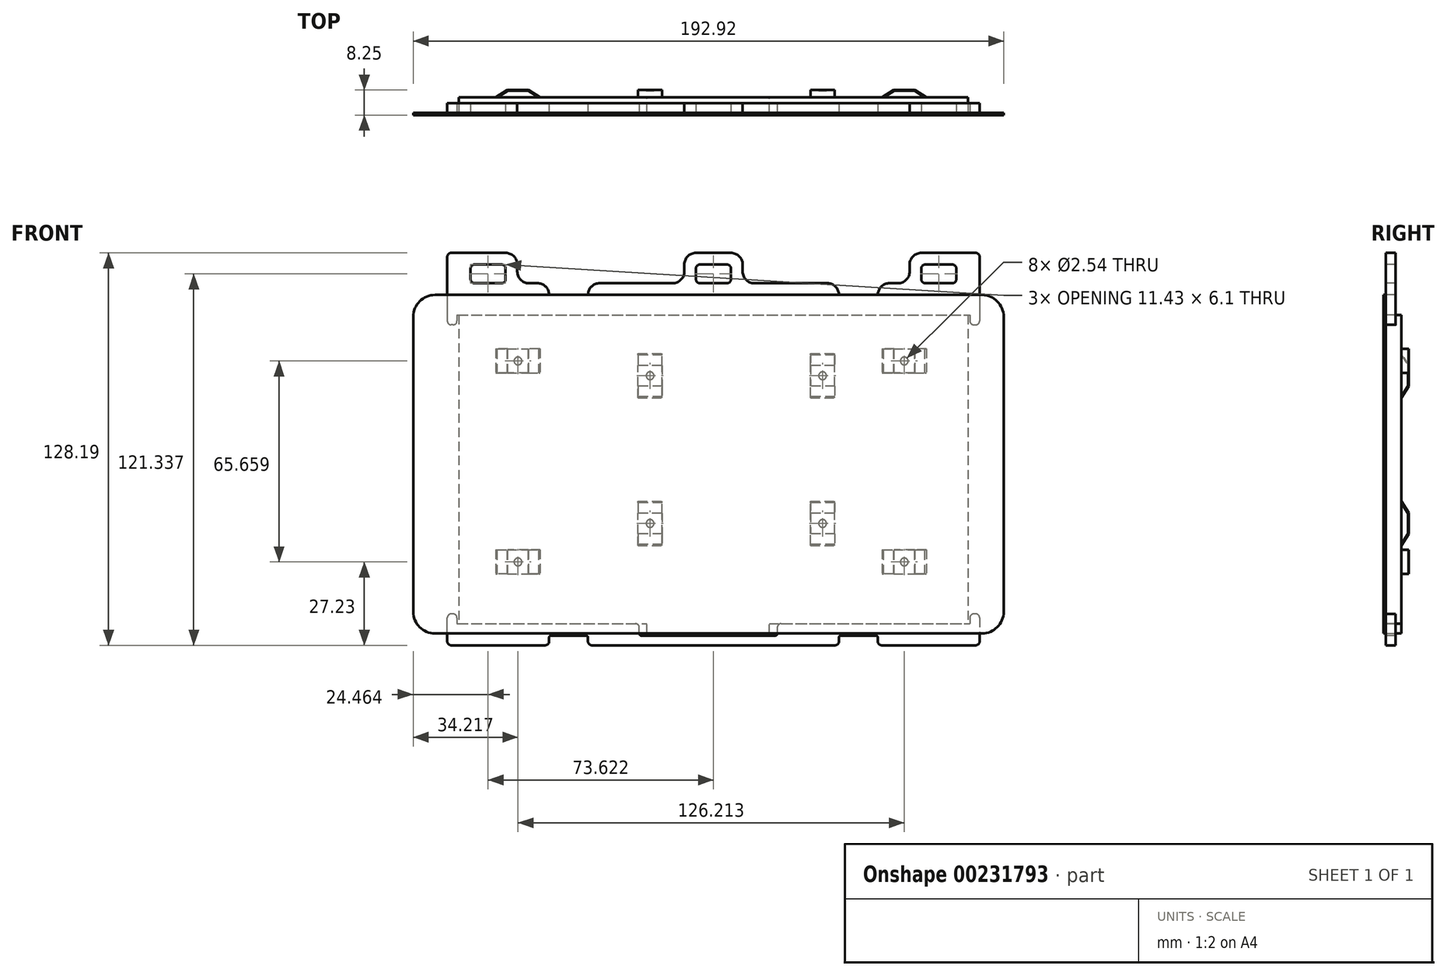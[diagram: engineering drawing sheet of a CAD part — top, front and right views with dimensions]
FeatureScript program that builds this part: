
annotation { "Feature Type Name" : "Feature", "Feature Type Description" : "" }
export const myFeature = defineFeature(function(context is Context, id is Id, definition is map)
    precondition{}
    {
        {
            var Q0;
            Q0=qCreatedBy(makeId("Front.planeOp"),FACE);
            var sketch = newSketch(context, id + "F0", { "sketchPlane" : qUnion([Q0])});
            skLineSegment(sketch, "E0.bottom", {"start": v(89.34, 55.3) * mm, "end": v(-89.34, 55.3) * mm});
            skLineSegment(sketch, "E0.top", {"start": v(89.34, -55.3) * mm, "end": v(-89.34, -55.3) * mm});
            skLineSegment(sketch, "E0.left", {"start": v(96.46, 48.2) * mm, "end": v(96.46, -48.2) * mm});
            skLineSegment(sketch, "E0.right", {"start": v(-96.46, 48.2) * mm, "end": v(-96.46, -48.2) * mm});
            skPoint(sketch, "E0.middle", {"position": v(0, 0) * mm});
            skPoint(sketch, "E1.visualSharp", {"position": v(-96.46, 55.3) * mm});
            skArc(sketch, "E1.filletArc", {"start": v(-89.34, 55.3) * mm, "mid": v(-94.37, 53.23) * mm, "end": v(-96.46, 48.2) * mm});
            skPoint(sketch, "E2.visualSharp", {"position": v(-96.46, -55.3) * mm});
            skArc(sketch, "E2.filletArc", {"start": v(-96.46, -48.2) * mm, "mid": v(-94.37, -53.23) * mm, "end": v(-89.34, -55.3) * mm});
            skPoint(sketch, "E3.visualSharp", {"position": v(96.46, -55.3) * mm});
            skArc(sketch, "E3.filletArc", {"start": v(89.34, -55.3) * mm, "mid": v(94.37, -53.23) * mm, "end": v(96.46, -48.2) * mm});
            skPoint(sketch, "E4.visualSharp", {"position": v(96.46, 55.3) * mm});
            skArc(sketch, "E4.filletArc", {"start": v(96.46, 48.2) * mm, "mid": v(94.37, 53.23) * mm, "end": v(89.34, 55.3) * mm});
            skSolve(sketch);
        }
        {
            var Q0;
            Q0=qSketchRegion(id+"F0",true);
            extrude(context, id + "F1", {"entities" : qUnion([Q0]), "depth" : 0.76 * mm});
        }
        {
            var Q0;
            Q0=makeQuery(id+"F1.opExtrude","CAP_FACE",FACE,{"disambiguationData":[OSD([sQuery(id+"F0.wireOp",EDGE,"E0.bottom"),sQuery(id+"F0.wireOp",EDGE,"E0.top"),sQuery(id+"F0.wireOp",EDGE,"E0.left"),sQuery(id+"F0.wireOp",EDGE,"E0.right"),sQuery(id+"F0.wireOp",EDGE,"E1.filletArc"),sQuery(id+"F0.wireOp",EDGE,"E2.filletArc"),sQuery(id+"F0.wireOp",EDGE,"E3.filletArc"),sQuery(id+"F0.wireOp",EDGE,"E4.filletArc")])],"isStart":true});
            var sketch = newSketch(context, id + "F2", { "sketchPlane" : qUnion([Q0])});
            skLineSegment(sketch, "E5.bottom", {"start": v(81.52, 48.7) * mm, "end": v(-84.77, 48.7) * mm});
            skLineSegment(sketch, "E5.top", {"start": v(81.52, -52.1) * mm, "end": v(-84.77, -52.1) * mm});
            skLineSegment(sketch, "E5.left", {"start": v(81.52, 48.7) * mm, "end": v(81.52, -52.1) * mm});
            skLineSegment(sketch, "E5.right", {"start": v(-84.77, 48.7) * mm, "end": v(-84.77, -52.1) * mm});
            skPoint(sketch, "E5.middle", {"position": v(-1.63, -1.7) * mm});
            skSolve(sketch);
        }
        {
            var Q0;
            Q0=qSketchRegion(id+"F2",true);
            extrude(context, id + "F3", {"entities" : qUnion([Q0]), "operationType" : NewBodyOperationType.ADD, "depth" : 5.08 * mm});
        }
        {
            var Q0;
            Q0=makeQuery(id+"F3.opExtrude","CAP_FACE",FACE,{"disambiguationData":[OSD([sQuery(id+"F2.wireOp",EDGE,"E5.bottom"),sQuery(id+"F2.wireOp",EDGE,"E5.top"),sQuery(id+"F2.wireOp",EDGE,"E5.left"),sQuery(id+"F2.wireOp",EDGE,"E5.right")])],"isStart":false});
            var sketch = newSketch(context, id + "F4", { "sketchPlane" : qUnion([Q0])});
            skLineSegment(sketch, "E6.bottom", {"start": v(-56.73, 37.66) * mm, "end": v(-71.2, 37.66) * mm});
            skLineSegment(sketch, "E6.top", {"start": v(-56.73, 29.78) * mm, "end": v(-71.2, 29.78) * mm});
            skLineSegment(sketch, "E6.left", {"start": v(-56.73, 37.66) * mm, "end": v(-56.73, 29.78) * mm});
            skLineSegment(sketch, "E6.right", {"start": v(-71.2, 37.66) * mm, "end": v(-71.2, 29.78) * mm});
            skPoint(sketch, "E6.middle", {"position": v(-63.97, 33.72) * mm});
            skLineSegment(sketch, "E7.bottom", {"start": v(-56.73, -28) * mm, "end": v(-71.2, -28) * mm});
            skLineSegment(sketch, "E7.top", {"start": v(-56.73, -35.88) * mm, "end": v(-71.2, -35.88) * mm});
            skLineSegment(sketch, "E7.left", {"start": v(-56.73, -28) * mm, "end": v(-56.73, -35.88) * mm});
            skLineSegment(sketch, "E7.right", {"start": v(-71.2, -28) * mm, "end": v(-71.2, -35.88) * mm});
            skPoint(sketch, "E7.middle", {"position": v(-63.97, -31.94) * mm});
            skLineSegment(sketch, "E8.bottom", {"start": v(69.48, 37.66) * mm, "end": v(55, 37.66) * mm});
            skLineSegment(sketch, "E8.top", {"start": v(69.48, 29.78) * mm, "end": v(55, 29.78) * mm});
            skLineSegment(sketch, "E8.left", {"start": v(69.48, 37.66) * mm, "end": v(69.48, 29.78) * mm});
            skLineSegment(sketch, "E8.right", {"start": v(55, 37.66) * mm, "end": v(55, 29.78) * mm});
            skPoint(sketch, "E8.middle", {"position": v(62.24, 33.72) * mm});
            skLineSegment(sketch, "E9.bottom", {"start": v(69.48, -28) * mm, "end": v(55, -28) * mm});
            skLineSegment(sketch, "E9.top", {"start": v(69.48, -35.88) * mm, "end": v(55, -35.88) * mm});
            skLineSegment(sketch, "E9.left", {"start": v(69.48, -28) * mm, "end": v(69.48, -35.88) * mm});
            skLineSegment(sketch, "E9.right", {"start": v(55, -28) * mm, "end": v(55, -35.88) * mm});
            skPoint(sketch, "E9.middle", {"position": v(62.24, -31.94) * mm});
            skLineSegment(sketch, "E10.bottom", {"start": v(-33.35, 21.65) * mm, "end": v(-41.22, 21.65) * mm});
            skLineSegment(sketch, "E10.top", {"start": v(-33.35, 36.13) * mm, "end": v(-41.22, 36.13) * mm});
            skLineSegment(sketch, "E10.left", {"start": v(-33.35, 21.65) * mm, "end": v(-33.35, 36.13) * mm});
            skLineSegment(sketch, "E10.right", {"start": v(-41.22, 21.65) * mm, "end": v(-41.22, 36.13) * mm});
            skPoint(sketch, "E10.middle", {"position": v(-37.29, 28.89) * mm});
            skLineSegment(sketch, "E11.bottom", {"start": v(23.03, 21.65) * mm, "end": v(15.15, 21.65) * mm});
            skLineSegment(sketch, "E11.top", {"start": v(23.03, 36.13) * mm, "end": v(15.15, 36.13) * mm});
            skLineSegment(sketch, "E11.left", {"start": v(23.03, 21.65) * mm, "end": v(23.03, 36.13) * mm});
            skLineSegment(sketch, "E11.right", {"start": v(15.15, 21.65) * mm, "end": v(15.15, 36.13) * mm});
            skPoint(sketch, "E11.middle", {"position": v(19.09, 28.89) * mm});
            skLineSegment(sketch, "E12.bottom", {"start": v(-33.35, -26.6) * mm, "end": v(-41.22, -26.6) * mm});
            skLineSegment(sketch, "E12.top", {"start": v(-33.35, -12.13) * mm, "end": v(-41.22, -12.13) * mm});
            skLineSegment(sketch, "E12.left", {"start": v(-33.35, -26.6) * mm, "end": v(-33.35, -12.13) * mm});
            skLineSegment(sketch, "E12.right", {"start": v(-41.22, -26.6) * mm, "end": v(-41.22, -12.13) * mm});
            skPoint(sketch, "E12.middle", {"position": v(-37.29, -19.37) * mm});
            skLineSegment(sketch, "E13.bottom", {"start": v(23.03, -26.6) * mm, "end": v(15.15, -26.6) * mm});
            skLineSegment(sketch, "E13.top", {"start": v(23.03, -12.13) * mm, "end": v(15.15, -12.13) * mm});
            skLineSegment(sketch, "E13.left", {"start": v(23.03, -26.6) * mm, "end": v(23.03, -12.13) * mm});
            skLineSegment(sketch, "E13.right", {"start": v(15.15, -26.6) * mm, "end": v(15.15, -12.13) * mm});
            skPoint(sketch, "E13.middle", {"position": v(19.09, -19.37) * mm});
            skLineSegment(sketch, "E14.bottom", {"start": v(-63.97, 33.72) * mm, "end": v(62.24, 33.72) * mm, "construction": true});
            skLineSegment(sketch, "E14.top", {"start": v(-63.97, -31.94) * mm, "end": v(62.24, -31.94) * mm, "construction": true});
            skLineSegment(sketch, "E14.left", {"start": v(-63.97, 33.72) * mm, "end": v(-63.97, -31.94) * mm, "construction": true});
            skLineSegment(sketch, "E14.right", {"start": v(62.24, 33.72) * mm, "end": v(62.24, -31.94) * mm, "construction": true});
            skLineSegment(sketch, "E15.bottom", {"start": v(-37.29, 28.89) * mm, "end": v(19.09, 28.89) * mm, "construction": true});
            skLineSegment(sketch, "E15.top", {"start": v(-37.29, -19.37) * mm, "end": v(19.09, -19.37) * mm, "construction": true});
            skLineSegment(sketch, "E15.left", {"start": v(-37.29, 28.89) * mm, "end": v(-37.29, -19.37) * mm, "construction": true});
            skLineSegment(sketch, "E15.right", {"start": v(19.09, 28.89) * mm, "end": v(19.09, -19.37) * mm, "construction": true});
            skCircle(sketch, "E16", {"center": v(-63.97, 33.72) * mm, "radius": 1.27 * mm});
            skCircle(sketch, "E17", {"center": v(62.24, 33.72) * mm, "radius": 1.27 * mm});
            skCircle(sketch, "E18", {"center": v(19.09, 28.89) * mm, "radius": 1.27 * mm});
            skCircle(sketch, "E19", {"center": v(-37.29, 28.89) * mm, "radius": 1.27 * mm});
            skCircle(sketch, "E20", {"center": v(-37.29, -19.37) * mm, "radius": 1.27 * mm});
            skCircle(sketch, "E21", {"center": v(19.09, -19.37) * mm, "radius": 1.27 * mm});
            skCircle(sketch, "E22", {"center": v(62.24, -31.94) * mm, "radius": 1.27 * mm});
            skCircle(sketch, "E23", {"center": v(-63.97, -31.94) * mm, "radius": 1.27 * mm});
            skSolve(sketch);
        }
        {
            var Q0;
            Q0=qSketchRegion(id+"F4",true);
            extrude(context, id + "F5", {"entities" : qUnion([Q0]), "operationType" : NewBodyOperationType.ADD, "depth" : 2.41 * mm});
        }
        {
            var Q0;
            Q0=makeQuery(id+"F5.opExtrude","CAP_EDGE",EDGE,{"disambiguationData":[OSD([sQuery(id+"F4.wireOp",EDGE,"E6.left")])],"isStart":false});
            var Q1;
            Q1=makeQuery(id+"F5.opExtrude","CAP_EDGE",EDGE,{"disambiguationData":[OSD([sQuery(id+"F4.wireOp",EDGE,"E7.left")])],"isStart":false});
            var Q2;
            Q2=makeQuery(id+"F5.opExtrude","CAP_EDGE",EDGE,{"disambiguationData":[OSD([sQuery(id+"F4.wireOp",EDGE,"E12.bottom")])],"isStart":false});
            var Q3;
            Q3=makeQuery(id+"F5.opExtrude","CAP_EDGE",EDGE,{"disambiguationData":[OSD([sQuery(id+"F4.wireOp",EDGE,"E10.bottom")])],"isStart":false});
            var Q4;
            Q4=makeQuery(id+"F5.opExtrude","CAP_EDGE",EDGE,{"disambiguationData":[OSD([sQuery(id+"F4.wireOp",EDGE,"E13.bottom")])],"isStart":false});
            var Q5;
            Q5=makeQuery(id+"F5.opExtrude","CAP_EDGE",EDGE,{"disambiguationData":[OSD([sQuery(id+"F4.wireOp",EDGE,"E11.bottom")])],"isStart":false});
            var Q6;
            Q6=makeQuery(id+"F5.opExtrude","CAP_EDGE",EDGE,{"disambiguationData":[OSD([sQuery(id+"F4.wireOp",EDGE,"E8.left")])],"isStart":false});
            var Q7;
            Q7=makeQuery(id+"F5.opExtrude","CAP_EDGE",EDGE,{"disambiguationData":[OSD([sQuery(id+"F4.wireOp",EDGE,"E9.left")])],"isStart":false});
            var Q8;
            Q8=makeQuery(id+"F5.opExtrude","CAP_EDGE",EDGE,{"disambiguationData":[OSD([sQuery(id+"F4.wireOp",EDGE,"E6.right")])],"isStart":false});
            chamfer(context, id + "F6", {"entities" : qUnion([Q0, Q1, Q2, Q3, Q4, Q5, Q6, Q7, Q8]), "chamferType" : ChamferType.TWO_OFFSETS, "width1" : 2.41 * mm, "oppositeDirection" : false, "width2" : 3.8 * mm, "tangentPropagation" : true});
        }
        {
            var Q0;
            Q0=makeQuery(id+"F5.opExtrude","CAP_EDGE",EDGE,{"disambiguationData":[OSD([sQuery(id+"F4.wireOp",EDGE,"E10.top")])],"isStart":false});
            var Q1;
            Q1=makeQuery(id+"F5.opExtrude","CAP_EDGE",EDGE,{"disambiguationData":[OSD([sQuery(id+"F4.wireOp",EDGE,"E7.right")])],"isStart":false});
            var Q2;
            Q2=makeQuery(id+"F5.opExtrude","CAP_EDGE",EDGE,{"disambiguationData":[OSD([sQuery(id+"F4.wireOp",EDGE,"E12.top")])],"isStart":false});
            var Q3;
            Q3=makeQuery(id+"F5.opExtrude","CAP_EDGE",EDGE,{"disambiguationData":[OSD([sQuery(id+"F4.wireOp",EDGE,"E13.top")])],"isStart":false});
            var Q4;
            Q4=makeQuery(id+"F5.opExtrude","CAP_EDGE",EDGE,{"disambiguationData":[OSD([sQuery(id+"F4.wireOp",EDGE,"E11.top")])],"isStart":false});
            var Q5;
            Q5=makeQuery(id+"F5.opExtrude","CAP_EDGE",EDGE,{"disambiguationData":[OSD([sQuery(id+"F4.wireOp",EDGE,"E8.right")])],"isStart":false});
            var Q6;
            Q6=makeQuery(id+"F5.opExtrude","CAP_EDGE",EDGE,{"disambiguationData":[OSD([sQuery(id+"F4.wireOp",EDGE,"E9.right")])],"isStart":false});
            chamfer(context, id + "F7", {"entities" : qUnion([Q0, Q1, Q2, Q3, Q4, Q5, Q6]), "chamferType" : ChamferType.TWO_OFFSETS, "width1" : 2.41 * mm, "oppositeDirection" : true, "width2" : 3.8 * mm, "tangentPropagation" : true});
        }
        {
            var Q0;
            Q0=makeQuery(id+"F5.opExtrude","SWEPT_FACE",FACE,{"disambiguationData":[OSD([sQuery(id+"F4.wireOp",EDGE,"E8.bottom")])]});
            var sketch = newSketch(context, id + "F8", { "sketchPlane" : qUnion([Q0])});
            skLineSegment(sketch, "E24.0", {"start": v(-69, 5.08) * mm, "end": v(-55.48, 5.08) * mm});
            skLineSegment(sketch, "E25.0", {"start": v(57.2, 5.08) * mm, "end": v(70.73, 5.08) * mm});
            skLineSegment(sketch, "E26.0", {"start": v(-65.6, 7.24) * mm, "end": v(-69, 5.08) * mm});
            skLineSegment(sketch, "E26.1", {"start": v(-65.6, 7.24) * mm, "end": v(-58.89, 7.24) * mm});
            skLineSegment(sketch, "E26.2", {"start": v(-55.48, 5.08) * mm, "end": v(-58.89, 7.24) * mm});
            skLineSegment(sketch, "E27.0", {"start": v(60.61, 7.24) * mm, "end": v(57.2, 5.08) * mm});
            skLineSegment(sketch, "E27.1", {"start": v(60.61, 7.24) * mm, "end": v(67.33, 7.24) * mm});
            skLineSegment(sketch, "E27.2", {"start": v(70.73, 5.08) * mm, "end": v(67.33, 7.24) * mm});
            skPoint(sketch, "E28.orphan", {"position": v(56.73, 5.08) * mm});
            skPoint(sketch, "E29.orphan", {"position": v(71.2, 5.08) * mm});
            skPoint(sketch, "E30.orphan", {"position": v(-55, 5.08) * mm});
            skPoint(sketch, "E31.orphan", {"position": v(-69.48, 5.08) * mm});
            skSolve(sketch);
        }
        {
            var Q0;
            Q0=qSketchRegion(id+"F8",true);
            var Q1;
            Q1=makeQuery(id+"F5.opExtrude","SWEPT_FACE",FACE,{"disambiguationData":[OSD([sQuery(id+"F4.wireOp",EDGE,"E9.top")])]});
            extrude(context, id + "F9", {"entities" : qUnion([Q0]), "operationType" : NewBodyOperationType.REMOVE, "endBound" : BoundingType.UP_TO_SURFACE, "oppositeDirection" : true, "endBoundEntityFace" : qUnion([Q1]), "depth" : 25.4 * mm});
        }
        {
            var Q0;
            Q0=makeQuery(id+"F5.opExtrude","SWEPT_FACE",FACE,{"disambiguationData":[OSD([sQuery(id+"F4.wireOp",EDGE,"E11.left")])]});
            var sketch = newSketch(context, id + "F10", { "sketchPlane" : qUnion([Q0])});
            skLineSegment(sketch, "E32.0", {"start": v(-5.08, -26.13) * mm, "end": v(-5.08, -12.6) * mm});
            skLineSegment(sketch, "E33.0", {"start": v(-5.08, 22.13) * mm, "end": v(-5.08, 35.65) * mm});
            skLineSegment(sketch, "E34.0", {"start": v(-7.24, -22.73) * mm, "end": v(-5.08, -26.13) * mm});
            skLineSegment(sketch, "E34.1", {"start": v(-7.24, -22.73) * mm, "end": v(-7.24, -16.01) * mm});
            skLineSegment(sketch, "E34.2", {"start": v(-5.08, -12.6) * mm, "end": v(-7.24, -16.01) * mm});
            skLineSegment(sketch, "E35.0", {"start": v(-7.24, 25.53) * mm, "end": v(-5.08, 22.13) * mm});
            skLineSegment(sketch, "E35.1", {"start": v(-7.24, 25.53) * mm, "end": v(-7.24, 32.25) * mm});
            skLineSegment(sketch, "E35.2", {"start": v(-5.08, 35.65) * mm, "end": v(-7.24, 32.25) * mm});
            skPoint(sketch, "E36.orphan", {"position": v(-5.08, -12.13) * mm});
            skPoint(sketch, "E37.orphan", {"position": v(-5.08, -26.6) * mm});
            skPoint(sketch, "E38.orphan", {"position": v(-5.08, 21.65) * mm});
            skPoint(sketch, "E39.orphan", {"position": v(-5.08, 36.13) * mm});
            skSolve(sketch);
        }
        {
            var Q0;
            Q0=qSketchRegion(id+"F10",true);
            var Q1;
            Q1=makeQuery(id+"F5.opExtrude","SWEPT_FACE",FACE,{"disambiguationData":[OSD([sQuery(id+"F4.wireOp",EDGE,"E12.right")])]});
            extrude(context, id + "F11", {"entities" : qUnion([Q0]), "operationType" : NewBodyOperationType.REMOVE, "endBound" : BoundingType.UP_TO_SURFACE, "oppositeDirection" : true, "endBoundEntityFace" : qUnion([Q1]), "depth" : 25.4 * mm});
        }
        {
            var Q0;
            Q0=makeQuery(id+"F3.opExtrude","SWEPT_FACE",FACE,{"disambiguationData":[OSD([sQuery(id+"F2.wireOp",EDGE,"E5.top")])]});
            var sketch = newSketch(context, id + "F12", { "sketchPlane" : qUnion([Q0])});
            skLineSegment(sketch, "E40.bottom", {"start": v(19.95, 0) * mm, "end": v(-20.05, 0) * mm});
            skLineSegment(sketch, "E40.top", {"start": v(19.95, -5.08) * mm, "end": v(-20.05, -5.08) * mm});
            skLineSegment(sketch, "E40.left", {"start": v(19.95, 0) * mm, "end": v(19.95, -5.08) * mm});
            skLineSegment(sketch, "E40.right", {"start": v(-20.05, 0) * mm, "end": v(-20.05, -5.08) * mm});
            skSolve(sketch);
        }
        {
            var Q0;
            Q0=qSketchRegion(id+"F12",true);
            var Q1;
            Q1=makeQuery(id+"F1.opExtrude","SWEPT_FACE",FACE,{"disambiguationData":[OSD([sQuery(id+"F0.wireOp",EDGE,"E0.top")])]});
            extrude(context, id + "F13", {"entities" : qUnion([Q0]), "operationType" : NewBodyOperationType.ADD, "endBound" : BoundingType.UP_TO_SURFACE, "endBoundEntityFace" : qUnion([Q1]), "depth" : 25.4 * mm});
        }
        {
            var Q0;
            Q0=makeQuery(id+"F1.opExtrude","CAP_FACE",FACE,{"disambiguationData":[OSD([sQuery(id+"F0.wireOp",EDGE,"E0.bottom"),sQuery(id+"F0.wireOp",EDGE,"E0.top"),sQuery(id+"F0.wireOp",EDGE,"E0.left"),sQuery(id+"F0.wireOp",EDGE,"E0.right"),sQuery(id+"F0.wireOp",EDGE,"E1.filletArc"),sQuery(id+"F0.wireOp",EDGE,"E2.filletArc"),sQuery(id+"F0.wireOp",EDGE,"E3.filletArc"),sQuery(id+"F0.wireOp",EDGE,"E4.filletArc")])],"isStart":true});
            var sketch = newSketch(context, id + "F14", { "sketchPlane" : qUnion([Q0])});
            skLineSegment(sketch, "E41.0", {"start": v(81.52, 48.7) * mm, "end": v(-84.77, 48.7) * mm});
            skLineSegment(sketch, "E42", {"start": v(-84.77, 48.7) * mm, "end": v(-84.77, 59.12) * mm});
            skLineSegment(sketch, "E43", {"start": v(-61.91, 59.12) * mm, "end": v(-59.14, 59.12) * mm});
            skLineSegment(sketch, "E44", {"start": v(81.52, 59.12) * mm, "end": v(81.52, 48.7) * mm});
            skLineSegment(sketch, "E45.top", {"start": v(-55.33, 55.3) * mm, "end": v(-42.63, 55.3) * mm});
            skLineSegment(sketch, "E45.left", {"start": v(-55.33, 55.3) * mm, "end": v(-55.33, 55.3) * mm});
            skLineSegment(sketch, "E45.right", {"start": v(-42.63, 55.3) * mm, "end": v(-42.63, 55.3) * mm});
            skLineSegment(sketch, "E46.0", {"start": v(-56.73, 37.66) * mm, "end": v(-56.73, 29.78) * mm, "construction": true});
            skPoint(sketch, "E47.0", {"position": v(-41.22, 28.89) * mm});
            skLineSegment(sketch, "E48.0", {"start": v(-41.22, 25.46) * mm, "end": v(-41.22, 32.32) * mm, "construction": true});
            skLineSegment(sketch, "E49", {"start": v(-56.73, 29.78) * mm, "end": v(-41.22, 29.78) * mm, "construction": true});
            skPoint(sketch, "E50", {"position": v(-48.98, 29.78) * mm});
            skLineSegment(sketch, "E51", {"start": v(-48.98, 77.85) * mm, "end": v(-48.98, -69.59) * mm, "construction": true});
            skLineSegment(sketch, "E52", {"start": v(-55.33, 57.21) * mm, "end": v(-42.63, 57.21) * mm, "construction": true});
            skPoint(sketch, "E53", {"position": v(-48.98, 57.21) * mm});
            skLineSegment(sketch, "E54", {"start": v(-1.63, 59.12) * mm, "end": v(-1.63, -121.25) * mm, "construction": true});
            skLineSegment(sketch, "E55.trimOffspring", {"start": v(-38.82, 59.12) * mm, "end": v(-14.96, 59.12) * mm});
            skLineSegment(sketch, "E56.MirrorCS", {"start": v(39.38, 55.3) * mm, "end": v(39.38, 55.3) * mm});
            skLineSegment(sketch, "E57.MirrorCS", {"start": v(52.08, 55.3) * mm, "end": v(39.38, 55.3) * mm});
            skLineSegment(sketch, "E58.MirrorCS", {"start": v(52.08, 55.3) * mm, "end": v(52.08, 55.3) * mm});
            skLineSegment(sketch, "E59.trimOffspring", {"start": v(55.89, 59.12) * mm, "end": v(58.66, 59.12) * mm});
            skLineSegment(sketch, "E60.bottom", {"start": v(-7.34, 69.02) * mm, "end": v(4.09, 69.02) * mm});
            skLineSegment(sketch, "E60.left", {"start": v(-11.15, 65.21) * mm, "end": v(-11.15, 62.93) * mm});
            skLineSegment(sketch, "E60.right", {"start": v(7.9, 65.21) * mm, "end": v(7.9, 62.93) * mm});
            skPoint(sketch, "E61", {"position": v(-1.63, 59.12) * mm});
            skLineSegment(sketch, "E62.top", {"start": v(-80.96, 69.02) * mm, "end": v(-69.53, 69.02) * mm});
            skLineSegment(sketch, "E62.left", {"start": v(-84.77, 59.12) * mm, "end": v(-84.77, 65.21) * mm});
            skLineSegment(sketch, "E62.right", {"start": v(-65.72, 62.93) * mm, "end": v(-65.72, 65.21) * mm});
            skLineSegment(sketch, "E63.top", {"start": v(77.71, 69.02) * mm, "end": v(66.28, 69.02) * mm});
            skLineSegment(sketch, "E63.left", {"start": v(81.52, 59.12) * mm, "end": v(81.52, 65.21) * mm});
            skLineSegment(sketch, "E63.right", {"start": v(62.47, 62.93) * mm, "end": v(62.47, 65.21) * mm});
            skLineSegment(sketch, "E64.trimOffspring", {"start": v(11.7, 59.12) * mm, "end": v(35.57, 59.12) * mm});
            skPoint(sketch, "E65.visualSharp", {"position": v(-65.72, 59.12) * mm});
            skArc(sketch, "E65.filletArc", {"start": v(-65.72, 62.93) * mm, "mid": v(-64.6, 60.23) * mm, "end": v(-61.91, 59.12) * mm});
            skPoint(sketch, "E66.visualSharp", {"position": v(-11.15, 59.12) * mm});
            skArc(sketch, "E66.filletArc", {"start": v(-14.96, 59.12) * mm, "mid": v(-12.27, 60.23) * mm, "end": v(-11.15, 62.93) * mm});
            skPoint(sketch, "E67.visualSharp", {"position": v(7.9, 59.12) * mm});
            skArc(sketch, "E67.filletArc", {"start": v(7.9, 62.93) * mm, "mid": v(9.02, 60.23) * mm, "end": v(11.7, 59.12) * mm});
            skPoint(sketch, "E68.visualSharp", {"position": v(62.47, 59.12) * mm});
            skArc(sketch, "E68.filletArc", {"start": v(58.66, 59.12) * mm, "mid": v(61.36, 60.23) * mm, "end": v(62.47, 62.93) * mm});
            skPoint(sketch, "E69.visualSharp", {"position": v(7.9, 69.02) * mm});
            skArc(sketch, "E69.filletArc", {"start": v(7.9, 65.21) * mm, "mid": v(6.78, 67.9) * mm, "end": v(4.09, 69.02) * mm});
            skPoint(sketch, "E70.visualSharp", {"position": v(-11.15, 69.02) * mm});
            skArc(sketch, "E70.filletArc", {"start": v(-7.34, 69.02) * mm, "mid": v(-10.03, 67.9) * mm, "end": v(-11.15, 65.21) * mm});
            skPoint(sketch, "E71.visualSharp", {"position": v(-65.72, 69.02) * mm});
            skArc(sketch, "E71.filletArc", {"start": v(-65.72, 65.21) * mm, "mid": v(-66.84, 67.9) * mm, "end": v(-69.53, 69.02) * mm});
            skPoint(sketch, "E72.visualSharp", {"position": v(-84.77, 69.02) * mm});
            skArc(sketch, "E72.filletArc", {"start": v(-80.96, 69.02) * mm, "mid": v(-83.66, 67.9) * mm, "end": v(-84.77, 65.21) * mm});
            skPoint(sketch, "E73.visualSharp", {"position": v(62.47, 69.02) * mm});
            skArc(sketch, "E73.filletArc", {"start": v(66.28, 69.02) * mm, "mid": v(63.59, 67.9) * mm, "end": v(62.47, 65.21) * mm});
            skPoint(sketch, "E74.visualSharp", {"position": v(81.52, 69.02) * mm});
            skArc(sketch, "E74.filletArc", {"start": v(81.52, 65.21) * mm, "mid": v(80.4, 67.9) * mm, "end": v(77.71, 69.02) * mm});
            skPoint(sketch, "E75.visualSharp", {"position": v(39.38, 59.12) * mm});
            skArc(sketch, "E75.filletArc", {"start": v(39.38, 55.3) * mm, "mid": v(38.26, 58) * mm, "end": v(35.57, 59.12) * mm});
            skPoint(sketch, "E76.visualSharp", {"position": v(-42.63, 59.12) * mm});
            skArc(sketch, "E76.filletArc", {"start": v(-38.82, 59.12) * mm, "mid": v(-41.51, 58) * mm, "end": v(-42.63, 55.3) * mm});
            skPoint(sketch, "E77.centerSnap0", {"position": v(-84.77, 62.17) * mm});
            skPoint(sketch, "E77.centerSnap1", {"position": v(-75.25, 69.02) * mm});
            skPoint(sketch, "E78.centerSnap0", {"position": v(-11.15, 64.07) * mm});
            skPoint(sketch, "E79.centerSnap0", {"position": v(62.47, 64.07) * mm});
            skPoint(sketch, "E79.centerSnap1", {"position": v(72, 69.02) * mm});
            skPoint(sketch, "E80.centerSnap0", {"position": v(-1.63, 69.02) * mm});
            skPoint(sketch, "E81.visualSharp", {"position": v(-55.33, 59.12) * mm});
            skArc(sketch, "E81.filletArc", {"start": v(-55.33, 55.3) * mm, "mid": v(-56.44, 58) * mm, "end": v(-59.14, 59.12) * mm});
            skPoint(sketch, "E82.visualSharp", {"position": v(52.08, 59.12) * mm});
            skArc(sketch, "E82.filletArc", {"start": v(55.89, 59.12) * mm, "mid": v(53.2, 58) * mm, "end": v(52.08, 55.3) * mm});
            skLineSegment(sketch, "E83", {"start": v(-84.77, 62.17) * mm, "end": v(81.52, 62.17) * mm, "construction": true});
            skLineSegment(sketch, "E84.bottom", {"start": v(-70.8, 65.21) * mm, "end": v(-79.7, 65.21) * mm});
            skLineSegment(sketch, "E84.top", {"start": v(-70.8, 59.12) * mm, "end": v(-79.7, 59.12) * mm});
            skLineSegment(sketch, "E84.left", {"start": v(-69.53, 63.94) * mm, "end": v(-69.53, 60.39) * mm});
            skLineSegment(sketch, "E84.right", {"start": v(-80.96, 63.94) * mm, "end": v(-80.96, 60.39) * mm});
            skPoint(sketch, "E84.middle", {"position": v(-75.25, 62.17) * mm});
            skLineSegment(sketch, "E85.bottom", {"start": v(2.82, 65.21) * mm, "end": v(-6.07, 65.21) * mm});
            skLineSegment(sketch, "E85.top", {"start": v(2.82, 59.12) * mm, "end": v(-6.07, 59.12) * mm});
            skLineSegment(sketch, "E85.left", {"start": v(4.09, 63.94) * mm, "end": v(4.09, 60.39) * mm});
            skLineSegment(sketch, "E85.right", {"start": v(-7.34, 63.94) * mm, "end": v(-7.34, 60.39) * mm});
            skPoint(sketch, "E85.middle", {"position": v(-1.63, 62.17) * mm});
            skLineSegment(sketch, "E86.bottom", {"start": v(76.44, 65.21) * mm, "end": v(67.55, 65.21) * mm});
            skLineSegment(sketch, "E86.top", {"start": v(76.44, 59.12) * mm, "end": v(67.55, 59.12) * mm});
            skLineSegment(sketch, "E86.left", {"start": v(77.71, 63.94) * mm, "end": v(77.71, 60.39) * mm});
            skLineSegment(sketch, "E86.right", {"start": v(66.28, 63.94) * mm, "end": v(66.28, 60.39) * mm});
            skPoint(sketch, "E86.middle", {"position": v(72, 62.17) * mm});
            skArc(sketch, "E87.filletArc", {"start": v(-69.53, 63.94) * mm, "mid": v(-69.9, 64.84) * mm, "end": v(-70.8, 65.21) * mm});
            skPoint(sketch, "E88.visualSharp", {"position": v(-80.96, 59.12) * mm});
            skArc(sketch, "E88.filletArc", {"start": v(-80.96, 60.39) * mm, "mid": v(-80.6, 59.5) * mm, "end": v(-79.7, 59.12) * mm});
            skPoint(sketch, "E89.visualSharp", {"position": v(-69.53, 59.12) * mm});
            skArc(sketch, "E89.filletArc", {"start": v(-70.8, 59.12) * mm, "mid": v(-69.9, 59.5) * mm, "end": v(-69.53, 60.39) * mm});
            skArc(sketch, "E90.filletArc", {"start": v(-79.7, 65.21) * mm, "mid": v(-80.6, 64.84) * mm, "end": v(-80.96, 63.94) * mm});
            skArc(sketch, "E91.filletArc", {"start": v(-6.07, 65.21) * mm, "mid": v(-6.97, 64.84) * mm, "end": v(-7.34, 63.94) * mm});
            skArc(sketch, "E92.filletArc", {"start": v(4.09, 63.94) * mm, "mid": v(3.72, 64.84) * mm, "end": v(2.82, 65.21) * mm});
            skPoint(sketch, "E93.visualSharp", {"position": v(4.09, 59.12) * mm});
            skArc(sketch, "E93.filletArc", {"start": v(2.82, 59.12) * mm, "mid": v(3.72, 59.5) * mm, "end": v(4.09, 60.39) * mm});
            skPoint(sketch, "E94.visualSharp", {"position": v(-7.34, 59.12) * mm});
            skArc(sketch, "E94.filletArc", {"start": v(-7.34, 60.39) * mm, "mid": v(-6.97, 59.5) * mm, "end": v(-6.07, 59.12) * mm});
            skPoint(sketch, "E95.visualSharp", {"position": v(66.28, 59.12) * mm});
            skArc(sketch, "E95.filletArc", {"start": v(66.28, 60.39) * mm, "mid": v(66.65, 59.5) * mm, "end": v(67.55, 59.12) * mm});
            skPoint(sketch, "E96.visualSharp", {"position": v(77.71, 59.12) * mm});
            skArc(sketch, "E96.filletArc", {"start": v(76.44, 59.12) * mm, "mid": v(77.34, 59.5) * mm, "end": v(77.71, 60.39) * mm});
            skArc(sketch, "E97.filletArc", {"start": v(67.55, 65.21) * mm, "mid": v(66.65, 64.84) * mm, "end": v(66.28, 63.94) * mm});
            skArc(sketch, "E98.filletArc", {"start": v(77.71, 63.94) * mm, "mid": v(77.34, 64.84) * mm, "end": v(76.44, 65.21) * mm});
            skLineSegment(sketch, "E99.bottom", {"start": v(-84.77, 69.02) * mm, "end": v(-87.31, 69.02) * mm});
            skLineSegment(sketch, "E99.top", {"start": v(-86.68, 45.53) * mm, "end": v(-87.31, 45.53) * mm});
            skLineSegment(sketch, "E99.left", {"start": v(-84.77, 69.02) * mm, "end": v(-84.77, 48.7) * mm});
            skLineSegment(sketch, "E99.right", {"start": v(-88.58, 67.75) * mm, "end": v(-88.58, 46.8) * mm});
            skLineSegment(sketch, "E100", {"start": v(-84.77, 69.02) * mm, "end": v(-80.96, 69.02) * mm});
            skLineSegment(sketch, "E101.bottom", {"start": v(-84.77, 48.7) * mm, "end": v(-85.4, 48.7) * mm});
            skLineSegment(sketch, "E101.right", {"start": v(-85.4, 48.7) * mm, "end": v(-85.4, 46.8) * mm});
            skPoint(sketch, "E102.orphan", {"position": v(-84.77, 45.53) * mm});
            skLineSegment(sketch, "E103.MirrorCS", {"start": v(81.52, 69.02) * mm, "end": v(77.71, 69.02) * mm});
            skLineSegment(sketch, "E104.MirrorCS", {"start": v(81.52, 69.02) * mm, "end": v(84.06, 69.02) * mm});
            skLineSegment(sketch, "E105.MirrorCS", {"start": v(85.33, 67.75) * mm, "end": v(85.33, 46.8) * mm});
            skLineSegment(sketch, "E106.MirrorCS", {"start": v(83.43, 45.53) * mm, "end": v(84.06, 45.53) * mm});
            skLineSegment(sketch, "E107.MirrorCS", {"start": v(82.16, 48.7) * mm, "end": v(82.16, 46.8) * mm});
            skLineSegment(sketch, "E108.MirrorCS", {"start": v(81.52, 48.7) * mm, "end": v(82.16, 48.7) * mm});
            skPoint(sketch, "E109.visualSharp", {"position": v(85.33, 45.53) * mm});
            skArc(sketch, "E109.filletArc", {"start": v(84.06, 45.53) * mm, "mid": v(84.96, 45.9) * mm, "end": v(85.33, 46.8) * mm});
            skPoint(sketch, "E110.visualSharp", {"position": v(82.16, 45.53) * mm});
            skArc(sketch, "E110.filletArc", {"start": v(82.16, 46.8) * mm, "mid": v(82.53, 45.9) * mm, "end": v(83.43, 45.53) * mm});
            skPoint(sketch, "E111.visualSharp", {"position": v(85.33, 69.02) * mm});
            skArc(sketch, "E111.filletArc", {"start": v(85.33, 67.75) * mm, "mid": v(84.96, 68.65) * mm, "end": v(84.06, 69.02) * mm});
            skPoint(sketch, "E112.visualSharp", {"position": v(-88.58, 69.02) * mm});
            skArc(sketch, "E112.filletArc", {"start": v(-87.31, 69.02) * mm, "mid": v(-88.21, 68.65) * mm, "end": v(-88.58, 67.75) * mm});
            skPoint(sketch, "E113.visualSharp", {"position": v(-88.58, 45.53) * mm});
            skArc(sketch, "E113.filletArc", {"start": v(-88.58, 46.8) * mm, "mid": v(-88.21, 45.9) * mm, "end": v(-87.31, 45.53) * mm});
            skPoint(sketch, "E114.visualSharp", {"position": v(-85.4, 45.53) * mm});
            skArc(sketch, "E114.filletArc", {"start": v(-86.68, 45.53) * mm, "mid": v(-85.78, 45.9) * mm, "end": v(-85.4, 46.8) * mm});
            skSolve(sketch);
        }
        {
            var Q0;
            Q0 = qSketchRegion(id + "F14", true);
            extrude(context, id + "F15", {"entities" : qUnion([Q0]), "depth" : 3.17 * mm});
        }
        {
            var Q0;
            Q0=makeQuery(id+"F1.opExtrude","CAP_FACE",FACE,{"disambiguationData":[OSD([sQuery(id+"F0.wireOp",EDGE,"E0.bottom"),sQuery(id+"F0.wireOp",EDGE,"E0.top"),sQuery(id+"F0.wireOp",EDGE,"E0.left"),sQuery(id+"F0.wireOp",EDGE,"E0.right"),sQuery(id+"F0.wireOp",EDGE,"E1.filletArc"),sQuery(id+"F0.wireOp",EDGE,"E2.filletArc"),sQuery(id+"F0.wireOp",EDGE,"E3.filletArc"),sQuery(id+"F0.wireOp",EDGE,"E4.filletArc")])],"isStart":true});
            var sketch = newSketch(context, id + "F16", { "sketchPlane" : qUnion([Q0])});
            skLineSegment(sketch, "E115.bottom", {"start": v(-23.76, -52.1) * mm, "end": v(-84.14, -52.1) * mm});
            skLineSegment(sketch, "E115.top", {"start": v(-21.22, -56) * mm, "end": v(-83.54, -56) * mm});
            skLineSegment(sketch, "E115.left", {"start": v(-22.5, -53.37) * mm, "end": v(-22.5, -54.04) * mm});
            skLineSegment(sketch, "E115.right", {"start": v(-85.4, -53.37) * mm, "end": v(-85.4, -54.04) * mm});
            skLineSegment(sketch, "E116.bottom", {"start": v(23.86, -52.1) * mm, "end": v(80.89, -52.1) * mm});
            skLineSegment(sketch, "E116.top", {"start": v(21.32, -56) * mm, "end": v(80.06, -56) * mm});
            skLineSegment(sketch, "E116.left", {"start": v(22.6, -53.37) * mm, "end": v(22.6, -54.04) * mm});
            skLineSegment(sketch, "E116.right", {"start": v(82.16, -53.37) * mm, "end": v(82.16, -54.04) * mm});
            skPoint(sketch, "E117.visualSharp", {"position": v(-85.4, -52.1) * mm});
            skArc(sketch, "E117.filletArc", {"start": v(-84.14, -52.1) * mm, "mid": v(-85.04, -52.47) * mm, "end": v(-85.4, -53.37) * mm});
            skPoint(sketch, "E118.visualSharp", {"position": v(-85.4, -56) * mm});
            skPoint(sketch, "E119.visualSharp", {"position": v(-22.5, -52.1) * mm});
            skArc(sketch, "E119.filletArc", {"start": v(-22.5, -53.37) * mm, "mid": v(-22.86, -52.47) * mm, "end": v(-23.76, -52.1) * mm});
            skPoint(sketch, "E120.visualSharp", {"position": v(-22.5, -56) * mm});
            skPoint(sketch, "E121.visualSharp", {"position": v(22.6, -52.1) * mm});
            skArc(sketch, "E121.filletArc", {"start": v(23.86, -52.1) * mm, "mid": v(22.97, -52.47) * mm, "end": v(22.6, -53.37) * mm});
            skPoint(sketch, "E122.visualSharp", {"position": v(22.6, -56) * mm});
            skPoint(sketch, "E123.visualSharp", {"position": v(82.16, -52.1) * mm});
            skArc(sketch, "E123.filletArc", {"start": v(82.16, -53.37) * mm, "mid": v(81.78, -52.47) * mm, "end": v(80.89, -52.1) * mm});
            skPoint(sketch, "E124.visualSharp", {"position": v(82.16, -56) * mm});
            skLineSegment(sketch, "E125.0", {"start": v(-55.33, 55.3) * mm, "end": v(-42.63, 55.3) * mm, "construction": true});
            skLineSegment(sketch, "E126.0", {"start": v(39.38, 55.3) * mm, "end": v(52.08, 55.3) * mm, "construction": true});
            skLineSegment(sketch, "E127", {"start": v(-55.33, 55.3) * mm, "end": v(-55.33, -134.8) * mm, "construction": true});
            skLineSegment(sketch, "E128", {"start": v(-42.63, 55.3) * mm, "end": v(-42.63, -57.9) * mm, "construction": true});
            skLineSegment(sketch, "E129", {"start": v(39.38, 55.3) * mm, "end": v(39.38, -148.97) * mm, "construction": true});
            skLineSegment(sketch, "E130", {"start": v(52.08, 55.3) * mm, "end": v(52.08, -164.68) * mm, "construction": true});
            skLineSegment(sketch, "E131", {"start": v(-83.54, -56) * mm, "end": v(-85.4, -56) * mm});
            skLineSegment(sketch, "E132", {"start": v(-85.4, -56) * mm, "end": v(-85.4, -54.04) * mm});
            skLineSegment(sketch, "E133.bottom", {"start": v(-85.4, -56) * mm, "end": v(82.16, -56) * mm});
            skLineSegment(sketch, "E133.top", {"start": v(-84.14, -59.17) * mm, "end": v(-56.6, -59.17) * mm});
            skLineSegment(sketch, "E133.left", {"start": v(-85.4, -56) * mm, "end": v(-85.4, -57.9) * mm});
            skLineSegment(sketch, "E133.right", {"start": v(82.16, -56) * mm, "end": v(82.16, -57.9) * mm});
            skLineSegment(sketch, "E134", {"start": v(82.16, -54.04) * mm, "end": v(82.16, -56) * mm});
            skLineSegment(sketch, "E135", {"start": v(82.16, -56) * mm, "end": v(80.06, -56) * mm});
            skLineSegment(sketch, "E136", {"start": v(39.38, -57.9) * mm, "end": v(39.38, -56) * mm});
            skLineSegment(sketch, "E137", {"start": v(39.38, -56) * mm, "end": v(52.08, -56) * mm});
            skPoint(sketch, "E137.endSnap0", {"position": v(50.7, -56) * mm});
            skLineSegment(sketch, "E138", {"start": v(52.08, -56) * mm, "end": v(52.08, -57.9) * mm});
            skLineSegment(sketch, "E139", {"start": v(-55.33, -57.9) * mm, "end": v(-55.33, -56) * mm});
            skLineSegment(sketch, "E140", {"start": v(-55.33, -56) * mm, "end": v(-42.63, -56) * mm});
            skLineSegment(sketch, "E141", {"start": v(-42.63, -56) * mm, "end": v(-42.63, -63.33) * mm});
            skLineSegment(sketch, "E142.trimOffspring", {"start": v(-42.63, -63.33) * mm, "end": v(-42.63, -153.94) * mm, "construction": true});
            skLineSegment(sketch, "E143.trimOffspring", {"start": v(-41.36, -59.17) * mm, "end": v(38.1, -59.17) * mm});
            skLineSegment(sketch, "E144.trimOffspring", {"start": v(53.35, -59.17) * mm, "end": v(80.89, -59.17) * mm});
            skPoint(sketch, "E145.visualSharp", {"position": v(-85.4, -59.17) * mm});
            skArc(sketch, "E145.filletArc", {"start": v(-85.4, -57.9) * mm, "mid": v(-85.04, -58.8) * mm, "end": v(-84.14, -59.17) * mm});
            skPoint(sketch, "E146.visualSharp", {"position": v(-55.33, -59.17) * mm});
            skArc(sketch, "E146.filletArc", {"start": v(-56.6, -59.17) * mm, "mid": v(-55.7, -58.8) * mm, "end": v(-55.33, -57.9) * mm});
            skPoint(sketch, "E147.visualSharp", {"position": v(-42.63, -59.17) * mm});
            skArc(sketch, "E147.filletArc", {"start": v(-42.63, -57.9) * mm, "mid": v(-42.26, -58.8) * mm, "end": v(-41.36, -59.17) * mm});
            skPoint(sketch, "E148.visualSharp", {"position": v(39.38, -59.17) * mm});
            skArc(sketch, "E148.filletArc", {"start": v(38.1, -59.17) * mm, "mid": v(39, -58.8) * mm, "end": v(39.38, -57.9) * mm});
            skPoint(sketch, "E149.visualSharp", {"position": v(52.08, -59.17) * mm});
            skArc(sketch, "E149.filletArc", {"start": v(52.08, -57.9) * mm, "mid": v(52.45, -58.8) * mm, "end": v(53.35, -59.17) * mm});
            skPoint(sketch, "E150.visualSharp", {"position": v(82.16, -59.17) * mm});
            skArc(sketch, "E150.filletArc", {"start": v(80.89, -59.17) * mm, "mid": v(81.78, -58.8) * mm, "end": v(82.16, -57.9) * mm});
            skLineSegment(sketch, "E151", {"start": v(22.6, -54.04) * mm, "end": v(22.6, -56) * mm});
            skLineSegment(sketch, "E152", {"start": v(-22.5, -54.04) * mm, "end": v(-22.5, -56) * mm});
            skLineSegment(sketch, "E153.bottom", {"start": v(-87.31, -48.92) * mm, "end": v(-86.68, -48.92) * mm});
            skLineSegment(sketch, "E153.top", {"start": v(-87.31, -59.17) * mm, "end": v(-85.4, -59.17) * mm});
            skLineSegment(sketch, "E153.left", {"start": v(-88.58, -50.2) * mm, "end": v(-88.58, -57.9) * mm});
            skLineSegment(sketch, "E153.right", {"start": v(-85.4, -50.2) * mm, "end": v(-85.4, -59.17) * mm});
            skLineSegment(sketch, "E154.0", {"start": v(-84.77, 48.7) * mm, "end": v(-84.77, -52.1) * mm, "construction": true});
            skLineSegment(sketch, "E155.bottom", {"start": v(82.16, -59.17) * mm, "end": v(84.06, -59.17) * mm});
            skLineSegment(sketch, "E155.top", {"start": v(83.43, -48.92) * mm, "end": v(84.06, -48.92) * mm});
            skLineSegment(sketch, "E155.left", {"start": v(82.16, -59.17) * mm, "end": v(82.16, -50.2) * mm});
            skLineSegment(sketch, "E155.right", {"start": v(85.33, -57.9) * mm, "end": v(85.33, -50.2) * mm});
            skLineSegment(sketch, "E156", {"start": v(-85.4, -59.17) * mm, "end": v(-84.14, -59.17) * mm});
            skLineSegment(sketch, "E157", {"start": v(80.89, -59.17) * mm, "end": v(82.16, -59.17) * mm});
            skLineSegment(sketch, "E158", {"start": v(80.89, -52.1) * mm, "end": v(82.16, -52.1) * mm});
            skLineSegment(sketch, "E159", {"start": v(-84.14, -52.1) * mm, "end": v(-85.4, -52.1) * mm});
            skLineSegment(sketch, "E160", {"start": v(-85.4, -48.92) * mm, "end": v(82.16, -48.92) * mm, "construction": true});
            skPoint(sketch, "E161.visualSharp", {"position": v(-88.58, -48.92) * mm});
            skArc(sketch, "E161.filletArc", {"start": v(-87.31, -48.92) * mm, "mid": v(-88.21, -49.3) * mm, "end": v(-88.58, -50.2) * mm});
            skPoint(sketch, "E162.visualSharp", {"position": v(-85.4, -48.92) * mm});
            skArc(sketch, "E162.filletArc", {"start": v(-85.4, -50.2) * mm, "mid": v(-85.78, -49.3) * mm, "end": v(-86.68, -48.92) * mm});
            skPoint(sketch, "E163.visualSharp", {"position": v(-88.58, -59.17) * mm});
            skArc(sketch, "E163.filletArc", {"start": v(-88.58, -57.9) * mm, "mid": v(-88.21, -58.8) * mm, "end": v(-87.31, -59.17) * mm});
            skPoint(sketch, "E164.visualSharp", {"position": v(85.33, -48.92) * mm});
            skArc(sketch, "E164.filletArc", {"start": v(85.33, -50.2) * mm, "mid": v(84.96, -49.3) * mm, "end": v(84.06, -48.92) * mm});
            skPoint(sketch, "E165.visualSharp", {"position": v(82.16, -48.92) * mm});
            skArc(sketch, "E165.filletArc", {"start": v(83.43, -48.92) * mm, "mid": v(82.53, -49.3) * mm, "end": v(82.16, -50.2) * mm});
            skPoint(sketch, "E166.visualSharp", {"position": v(85.33, -59.17) * mm});
            skArc(sketch, "E166.filletArc", {"start": v(84.06, -59.17) * mm, "mid": v(84.96, -58.8) * mm, "end": v(85.33, -57.9) * mm});
            skLineSegment(sketch, "E167", {"start": v(23.86, -52.1) * mm, "end": v(82.16, -52.1) * mm});
            skLineSegment(sketch, "E168", {"start": v(82.16, -52.1) * mm, "end": v(82.16, -50.2) * mm});
            skSolve(sketch);
        }
        {
            var Q0;
            Q0=makeQuery(id+"F1.opExtrude","CAP_FACE",FACE,{"disambiguationData":[OSD([sQuery(id+"F0.wireOp",EDGE,"E0.bottom"),sQuery(id+"F0.wireOp",EDGE,"E0.top"),sQuery(id+"F0.wireOp",EDGE,"E0.left"),sQuery(id+"F0.wireOp",EDGE,"E0.right"),sQuery(id+"F0.wireOp",EDGE,"E1.filletArc"),sQuery(id+"F0.wireOp",EDGE,"E2.filletArc"),sQuery(id+"F0.wireOp",EDGE,"E3.filletArc"),sQuery(id+"F0.wireOp",EDGE,"E4.filletArc")])],"isStart":true});
            var sketch = newSketch(context, id + "F17", { "sketchPlane" : qUnion([Q0])});
            skLineSegment(sketch, "E169.0", {"start": v(-88.58, -50.2) * mm, "end": v(-88.58, -57.9) * mm});
            skPoint(sketch, "E170.0", {"position": v(-88.21, -58.8) * mm});
            skArc(sketch, "E171.0", {"start": v(-88.58, -57.9) * mm, "mid": v(-88.21, -58.8) * mm, "end": v(-87.31, -59.17) * mm});
            skPoint(sketch, "E172.0", {"position": v(-86.36, -59.17) * mm});
            skArc(sketch, "E173.0", {"start": v(-87.31, -48.92) * mm, "mid": v(-88.21, -49.3) * mm, "end": v(-88.58, -50.2) * mm});
            skArc(sketch, "E174.0", {"start": v(-85.4, -50.2) * mm, "mid": v(-85.78, -49.3) * mm, "end": v(-86.68, -48.92) * mm});
            skPoint(sketch, "E175.0", {"position": v(-87, -48.92) * mm});
            skLineSegment(sketch, "E176.0", {"start": v(-84.14, -52.1) * mm, "end": v(-85.4, -52.1) * mm});
            skLineSegment(sketch, "E177.0", {"start": v(-84.14, -59.17) * mm, "end": v(-56.6, -59.17) * mm});
            skPoint(sketch, "E178.0", {"position": v(-55.7, -58.8) * mm});
            skArc(sketch, "E179.0", {"start": v(-56.6, -59.17) * mm, "mid": v(-55.7, -58.8) * mm, "end": v(-55.33, -57.9) * mm});
            skLineSegment(sketch, "E180.0", {"start": v(-55.33, -57.9) * mm, "end": v(-55.33, -56) * mm});
            skArc(sketch, "E181.0", {"start": v(-22.5, -53.37) * mm, "mid": v(-22.86, -52.47) * mm, "end": v(-23.76, -52.1) * mm});
            skLineSegment(sketch, "E182.0", {"start": v(-41.36, -59.17) * mm, "end": v(38.1, -59.17) * mm});
            skArc(sketch, "E183.0", {"start": v(-42.63, -57.9) * mm, "mid": v(-42.26, -58.8) * mm, "end": v(-41.36, -59.17) * mm});
            skArc(sketch, "E184.0", {"start": v(83.43, -48.92) * mm, "mid": v(82.53, -49.3) * mm, "end": v(82.16, -50.2) * mm});
            skArc(sketch, "E185.0", {"start": v(85.33, -50.2) * mm, "mid": v(84.96, -49.3) * mm, "end": v(84.06, -48.92) * mm});
            skLineSegment(sketch, "E186.0", {"start": v(85.33, -57.9) * mm, "end": v(85.33, -50.2) * mm});
            skPoint(sketch, "E187.0", {"position": v(84.96, -58.8) * mm});
            skArc(sketch, "E188.0", {"start": v(84.06, -59.17) * mm, "mid": v(84.96, -58.8) * mm, "end": v(85.33, -57.9) * mm});
            skLineSegment(sketch, "E189.0", {"start": v(52.08, -56) * mm, "end": v(52.08, -57.9) * mm});
            skLineSegment(sketch, "E190.0", {"start": v(39.38, -57.9) * mm, "end": v(39.38, -56) * mm});
            skPoint(sketch, "E191.0", {"position": v(52.45, -58.8) * mm});
            skArc(sketch, "E192.0", {"start": v(52.08, -57.9) * mm, "mid": v(52.45, -58.8) * mm, "end": v(53.35, -59.17) * mm});
            skArc(sketch, "E193.0", {"start": v(38.1, -59.17) * mm, "mid": v(39, -58.8) * mm, "end": v(39.38, -57.9) * mm});
            skArc(sketch, "E194.0", {"start": v(23.86, -52.1) * mm, "mid": v(22.97, -52.47) * mm, "end": v(22.6, -53.37) * mm});
            skLineSegment(sketch, "E195", {"start": v(-22.5, -53.37) * mm, "end": v(-22.5, -56) * mm});
            skLineSegment(sketch, "E196", {"start": v(-22.5, -56) * mm, "end": v(22.6, -56) * mm});
            skLineSegment(sketch, "E197", {"start": v(22.6, -56) * mm, "end": v(22.6, -53.37) * mm});
            skLineSegment(sketch, "E198", {"start": v(23.86, -52.1) * mm, "end": v(82.16, -52.1) * mm});
            skLineSegment(sketch, "E199", {"start": v(53.35, -59.17) * mm, "end": v(84.06, -59.17) * mm});
            skLineSegment(sketch, "E200", {"start": v(39.38, -56) * mm, "end": v(52.08, -56) * mm});
            skLineSegment(sketch, "E201", {"start": v(-42.63, -57.9) * mm, "end": v(-42.63, -56) * mm});
            skLineSegment(sketch, "E202", {"start": v(-42.63, -56) * mm, "end": v(-55.33, -56) * mm});
            skLineSegment(sketch, "E203", {"start": v(-84.14, -52.1) * mm, "end": v(-23.76, -52.1) * mm});
            skLineSegment(sketch, "E204", {"start": v(-85.4, -50.2) * mm, "end": v(-85.4, -52.1) * mm});
            skLineSegment(sketch, "E205", {"start": v(-87.31, -59.17) * mm, "end": v(-84.14, -59.17) * mm});
            skLineSegment(sketch, "E206", {"start": v(-87.31, -48.92) * mm, "end": v(-86.68, -48.92) * mm});
            skLineSegment(sketch, "E207", {"start": v(82.16, -50.2) * mm, "end": v(82.16, -52.1) * mm});
            skLineSegment(sketch, "E208", {"start": v(83.43, -48.92) * mm, "end": v(84.06, -48.92) * mm});
            skSolve(sketch);
        }
        {
            var Q0;
            Q0 = qSketchRegion(id + "F17", true);
            extrude(context, id + "F18", {"entities" : qUnion([Q0]), "depth" : 3.17 * mm});
        }
        {
            var Q0;
            Q0=makeQuery(id+"F18.opExtrude","SWEPT_EDGE",EDGE,{"disambiguationData":[OSD([sQuery(id+"F17.wireOp",EDGE,"E195"),sQuery(id+"F17.wireOp",EDGE,"E196")])]});
            var Q1;
            Q1=makeQuery(id+"F18.opExtrude","SWEPT_EDGE",EDGE,{"disambiguationData":[OSD([sQuery(id+"F17.wireOp",EDGE,"E196"),sQuery(id+"F17.wireOp",EDGE,"E197")])]});
            var Q2;
            Q2=makeQuery(id+"F18.opExtrude","SWEPT_EDGE",EDGE,{"disambiguationData":[OSD([sQuery(id+"F17.wireOp",EDGE,"E180.0"),sQuery(id+"F17.wireOp",EDGE,"E202")])]});
            var Q3;
            Q3=makeQuery(id+"F18.opExtrude","SWEPT_EDGE",EDGE,{"disambiguationData":[OSD([sQuery(id+"F17.wireOp",EDGE,"E201"),sQuery(id+"F17.wireOp",EDGE,"E202")])]});
            var Q4;
            Q4=makeQuery(id+"F18.opExtrude","SWEPT_EDGE",EDGE,{"disambiguationData":[OSD([sQuery(id+"F17.wireOp",EDGE,"E189.0"),sQuery(id+"F17.wireOp",EDGE,"E200")])]});
            var Q5;
            Q5=makeQuery(id+"F18.opExtrude","SWEPT_EDGE",EDGE,{"disambiguationData":[OSD([sQuery(id+"F17.wireOp",EDGE,"E190.0"),sQuery(id+"F17.wireOp",EDGE,"E200")])]});
            var Q6;
            Q6=makeQuery(id+"F15.opExtrude","SWEPT_EDGE",EDGE,{"disambiguationData":[OSD([sQuery(id+"F0.wireOp",EDGE,"E0.bottom"),sQuery(id+"F14.wireOp",EDGE,"E45.top"),sQuery(id+"F14.wireOp",EDGE,"E76.filletArc")])]});
            var Q7;
            Q7=makeQuery(id+"F15.opExtrude","SWEPT_EDGE",EDGE,{"disambiguationData":[OSD([sQuery(id+"F0.wireOp",EDGE,"E0.bottom"),sQuery(id+"F14.wireOp",EDGE,"E45.top"),sQuery(id+"F14.wireOp",EDGE,"E81.filletArc")])]});
            var Q8;
            Q8=makeQuery(id+"F15.opExtrude","SWEPT_EDGE",EDGE,{"disambiguationData":[OSD([sQuery(id+"F0.wireOp",EDGE,"E0.bottom"),sQuery(id+"F14.wireOp",EDGE,"E57.MirrorCS"),sQuery(id+"F14.wireOp",EDGE,"E75.filletArc")])]});
            var Q9;
            Q9=makeQuery(id+"F15.opExtrude","SWEPT_EDGE",EDGE,{"disambiguationData":[OSD([sQuery(id+"F0.wireOp",EDGE,"E0.bottom"),sQuery(id+"F14.wireOp",EDGE,"E57.MirrorCS"),sQuery(id+"F14.wireOp",EDGE,"E82.filletArc")])]});
            fillet(context, id + "F19", {"entities" : qUnion([Q0, Q1, Q2, Q3, Q4, Q5, Q6, Q7, Q8, Q9]), "radius" : 0.64 * mm, "tangentPropagation" : true, "allowEdgeOverflow" : false});
        }
    });
